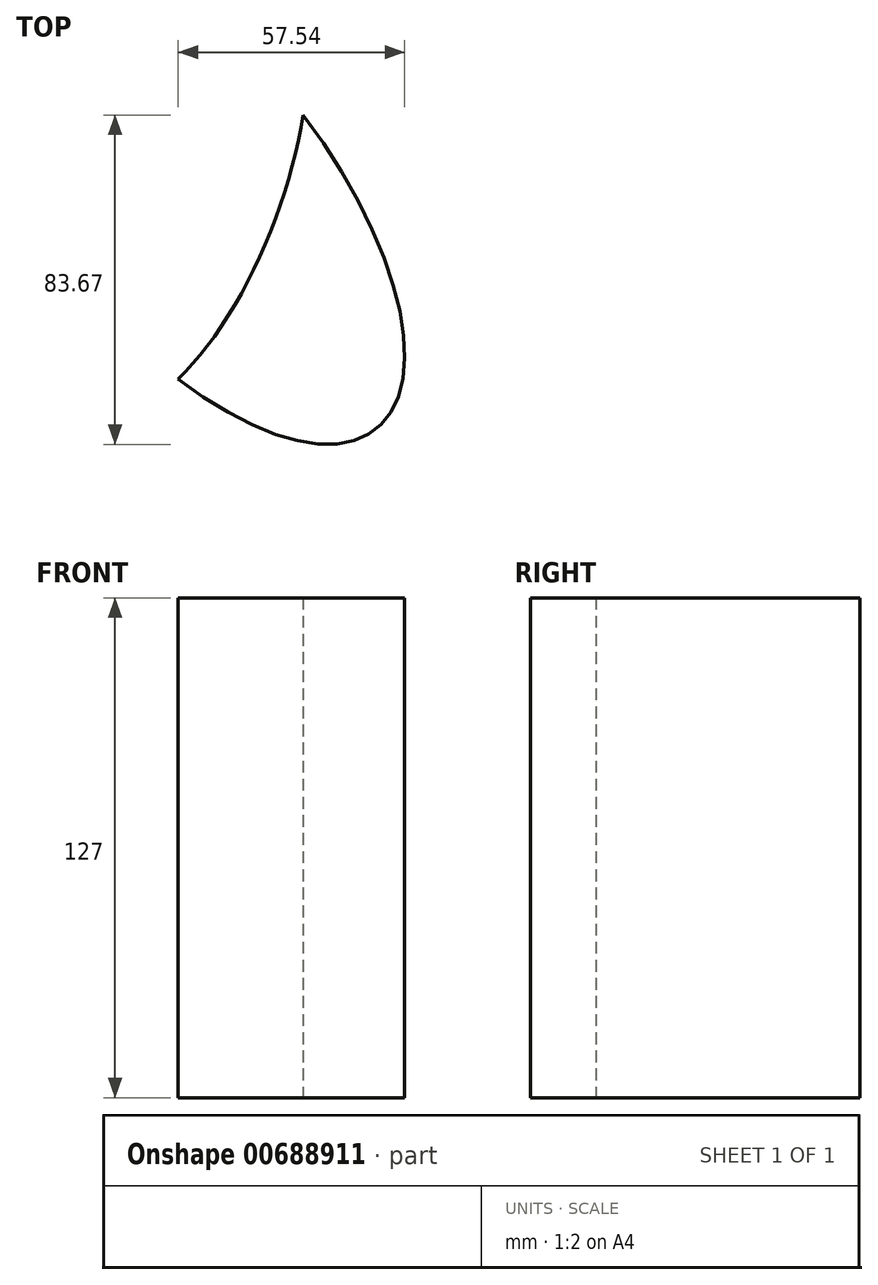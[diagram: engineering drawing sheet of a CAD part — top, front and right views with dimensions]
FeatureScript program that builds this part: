
annotation { "Feature Type Name" : "Feature", "Feature Type Description" : "" }
export const myFeature = defineFeature(function(context is Context, id is Id, definition is map)
    precondition{}
    {
        {
            var Q0;
            Q0=qCreatedBy(makeId("Top.planeOp"),FACE);
            var sketch = newSketch(context, id + "F0", { "sketchPlane" : qUnion([Q0])});
            skEllipse(sketch, "E0", {"center": v(23.52, -8.94) * mm, "majorRadius": 25.16 * mm, "minorRadius": 60.88 * mm, "majorAxis": v(-0.93, 0.36)});
            skEllipse(sketch, "E1", {"center": v(23.52, -8.94) * mm, "majorRadius": 78.9 * mm, "minorRadius": 35.53 * mm, "majorAxis": v(0.63, -0.78)});
            skSolve(sketch);
        }
        {
            var Q0;
            {var subQ0=sQuery(id+"F0.wireOp",EDGE,"E1");var subQ1=sQuery(id+"F0.wireOp",EDGE,"E0");var subQ2=makeQuery(id+"F0.imprint","INTERSECT",VERTEX,{"disambiguationData":[OD(0.0)],"derivedFrom":[subQ1,subQ0]});Q0=makeQuery(id+"F0.imprint","IMPRINT",FACE,{"disambiguationData":[TD([[makeQuery(id+"F0.imprint","IMPRINT",EDGE,{"disambiguationData":[TD([[subQ2,1.0]])],"derivedFrom":subQ1}),-1.0]])]});}
            extrude(context, id + "F1", {"entities" : qUnion([Q0]), "depth" : 127 * mm, "offsetDistance" : 25.4 * mm});
        }
    });
